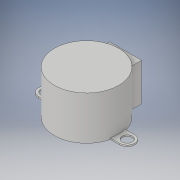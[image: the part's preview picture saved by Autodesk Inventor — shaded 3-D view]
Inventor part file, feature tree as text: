
AUTODESK INVENTOR PART (.ipt)
format: ipt  version: 2019 (Build 230136000, 136)  size: 135,168 bytes
history: native  units: mm
features: extrude x3, sketch x3
ambient origin geometry x8: Origin, YZ Plane, XZ Plane, XY Plane, X Axis, Y Axis, Z Axis, Center Point
bodies: Solide1 (feature_tree)
feature tree (6):
  extrude  "Extrusion1"  Depth=28.0mm
  extrude  "Extrusion2"  Depth=19.0mm TaperAngle=0.0deg
  extrude  "Extrusion3"  Depth=42.0mm
  sketch  "Esquisse1"
  sketch  "Esquisse2"
  sketch  "Esquisse3"
